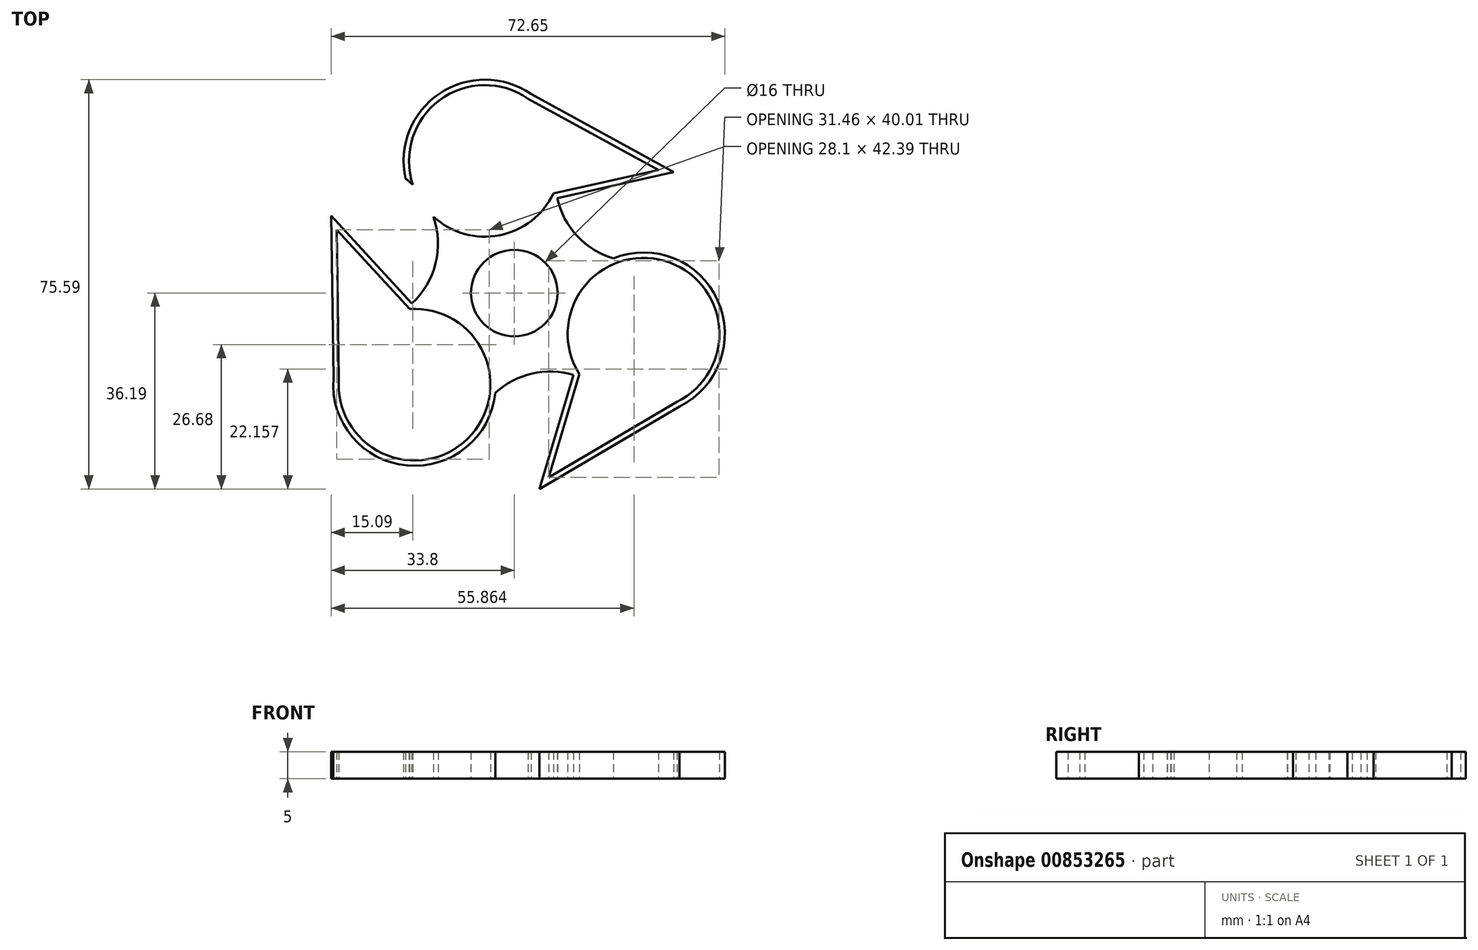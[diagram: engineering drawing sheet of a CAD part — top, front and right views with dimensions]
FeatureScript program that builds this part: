
annotation { "Feature Type Name" : "Feature", "Feature Type Description" : "" }
export const myFeature = defineFeature(function(context is Context, id is Id, definition is map)
    precondition{}
    {
        {
            var Q0;
            Q0=qCreatedBy(makeId("Top.planeOp"),FACE);
            var sketch = newSketch(context, id + "F0", { "sketchPlane" : qUnion([Q0])});
            skCircle(sketch, "E0", {"center": v(0, 0) * mm, "radius": 8 * mm});
            skCircle(sketch, "E1.cCircle", {"center": v(0, 0) * mm, "radius": 10 * mm, "construction": true});
            skLineSegment(sketch, "E1.0", {"start": v(-4.34, 19.52) * mm, "end": v(19.08, -6) * mm, "construction": true});
            skLineSegment(sketch, "E1.1", {"start": v(19.08, -6) * mm, "end": v(-14.73, -13.52) * mm, "construction": true});
            skLineSegment(sketch, "E1.2", {"start": v(-14.73, -13.52) * mm, "end": v(-4.34, 19.52) * mm, "construction": true});
            skPoint(sketch, "E1.0.midPoint", {"position": v(7.37, 6.76) * mm});
            skLineSegment(sketch, "E2", {"start": v(0, 0) * mm, "end": v(-9.6, 43.12) * mm, "construction": true});
            skLineSegment(sketch, "E3", {"start": v(0, 0) * mm, "end": v(53.7, -16.88) * mm, "construction": true});
            skLineSegment(sketch, "E4", {"start": v(0, 0) * mm, "end": v(-29.05, -26.67) * mm, "construction": true});
            skCircle(sketch, "E5", {"center": v(-5.43, 24.4) * mm, "radius": 15 * mm});
            skCircle(sketch, "E6", {"center": v(23.85, -7.5) * mm, "radius": 15 * mm});
            skCircle(sketch, "E7", {"center": v(-18.42, -16.9) * mm, "radius": 15 * mm});
            skLineSegment(sketch, "E8", {"start": v(-5.43, 24.4) * mm, "end": v(14.72, 28.89) * mm, "construction": true});
            skLineSegment(sketch, "E9", {"start": v(14.72, 28.89) * mm, "end": v(-26.3, 19.76) * mm, "construction": true});
            skLineSegment(sketch, "E10", {"start": v(-18.42, -16.9) * mm, "end": v(-38.8, 5.3) * mm, "construction": true});
            skLineSegment(sketch, "E11", {"start": v(-38.8, 5.3) * mm, "end": v(-1.77, -35.05) * mm, "construction": true});
            skLineSegment(sketch, "E12", {"start": v(23.85, -7.5) * mm, "end": v(30.7, 15.55) * mm, "construction": true});
            skLineSegment(sketch, "E13", {"start": v(30.7, 15.55) * mm, "end": v(16.82, -31.15) * mm, "construction": true});
            skArc(sketch, "E14", {"start": v(9.21, 27.66) * mm, "mid": v(11.46, 10.71) * mm, "end": v(28.12, 6.88) * mm});
            skArc(sketch, "E15", {"start": v(-28.56, -5.85) * mm, "mid": v(-14.75, 4.64) * mm, "end": v(-20.07, 21.14) * mm});
            skArc(sketch, "E16", {"start": v(19.58, -21.88) * mm, "mid": v(3.45, -14.83) * mm, "end": v(-8.28, -27.96) * mm});
            skCircle(sketch, "E17", {"center": v(-5.43, 24.4) * mm, "radius": 14 * mm});
            skCircle(sketch, "E18", {"center": v(23.85, -7.5) * mm, "radius": 14 * mm});
            skCircle(sketch, "E19", {"center": v(-18.42, -16.9) * mm, "radius": 14 * mm});
            skLineSegment(sketch, "E20", {"start": v(10.92, -15.1) * mm, "end": v(4.65, -36.2) * mm});
            skLineSegment(sketch, "E21", {"start": v(4.65, -36.2) * mm, "end": v(30.5, -20.95) * mm});
            skLineSegment(sketch, "E22", {"start": v(-18.92, -1.91) * mm, "end": v(-33.8, 14.3) * mm});
            skLineSegment(sketch, "E23", {"start": v(-33.8, 14.3) * mm, "end": v(-33.37, -15.7) * mm});
            skLineSegment(sketch, "E24", {"start": v(7.91, 17.55) * mm, "end": v(29.39, 22.33) * mm});
            skLineSegment(sketch, "E25", {"start": v(29.39, 22.33) * mm, "end": v(3.08, 36.75) * mm});
            skLineSegment(sketch, "E26", {"start": v(2.56, 35.9) * mm, "end": v(26.58, 22.73) * mm});
            skLineSegment(sketch, "E27", {"start": v(26.58, 22.73) * mm, "end": v(7.23, 18.42) * mm});
            skLineSegment(sketch, "E28", {"start": v(-32.37, -15.74) * mm, "end": v(-32.76, 11.69) * mm});
            skLineSegment(sketch, "E29", {"start": v(-32.76, 11.69) * mm, "end": v(-19.34, -2.94) * mm});
            skLineSegment(sketch, "E30", {"start": v(30.02, -20.07) * mm, "end": v(6.34, -34.04) * mm});
            skLineSegment(sketch, "E31", {"start": v(6.34, -34.04) * mm, "end": v(12, -14.96) * mm});
            skSolve(sketch);
        }
        {
            var Q0;
            {var subQ5=sQuery(id+"F0.wireOp",EDGE,"E6");var subQ6=makeQuery(id+"F0.imprint","INTERSECT",VERTEX,{"derivedFrom":[subQ5,sQuery(id+"F0.wireOp",EDGE,"E21")]});Q0=makeQuery(id+"F0.imprint","IMPRINT",FACE,{"disambiguationData":[TD([[makeQuery(id+"F0.imprint","IMPRINT",EDGE,{"disambiguationData":[TD([[subQ6,1.0]])],"derivedFrom":subQ5}),1.0]])]});}
            var Q1;
            {var subQ0=sQuery(id+"F0.wireOp",EDGE,"E20");Q1=makeQuery(id+"F0.imprint","IMPRINT",FACE,{"disambiguationData":[TD([[makeQuery(id+"F0.imprint","IMPRINT",EDGE,{"derivedFrom":subQ0}),1.0]])]});}
            var Q2;
            {var subQ0=sQuery(id+"F0.wireOp",EDGE,"E14");var subQ1=sQuery(id+"F0.wireOp",EDGE,"E6");var subQ2=makeQuery(id+"F0.imprint","INTERSECT",VERTEX,{"disambiguationData":[OD(0.0)],"derivedFrom":[subQ1,subQ0]});Q2=makeQuery(id+"F0.imprint","IMPRINT",FACE,{"disambiguationData":[TD([[makeQuery(id+"F0.imprint","IMPRINT",EDGE,{"disambiguationData":[TD([[subQ2,-1.0]])],"derivedFrom":subQ1}),1.0]])]});}
            var Q3;
            {var subQ1=sQuery(id+"F0.wireOp",EDGE,"E6");var subQ3=sQuery(id+"F0.wireOp",EDGE,"E31");var subQ4=makeQuery(id+"F0.imprint","INTERSECT",VERTEX,{"derivedFrom":[subQ1,subQ3]});Q3=makeQuery(id+"F0.imprint","IMPRINT",FACE,{"disambiguationData":[TD([[makeQuery(id+"F0.imprint","IMPRINT",EDGE,{"disambiguationData":[TD([[subQ4,-1.0]])],"derivedFrom":subQ3}),1.0]])]});}
            var Q4;
            {var subQ3=sQuery(id+"F0.wireOp",EDGE,"E14");var subQ6=sQuery(id+"F0.wireOp",EDGE,"E6");var subQ8=makeQuery(id+"F0.imprint","INTERSECT",VERTEX,{"disambiguationData":[OD(1.0)],"derivedFrom":[subQ6,subQ3]});Q4=makeQuery(id+"F0.imprint","IMPRINT",FACE,{"disambiguationData":[TD([[makeQuery(id+"F0.imprint","IMPRINT",EDGE,{"disambiguationData":[TD([[subQ8,-1.0]])],"derivedFrom":subQ3}),-1.0]])]});}
            var Q5;
            {var subQ1=sQuery(id+"F0.wireOp",EDGE,"E24");Q5=makeQuery(id+"F0.imprint","IMPRINT",FACE,{"disambiguationData":[TD([[makeQuery(id+"F0.imprint","IMPRINT",EDGE,{"derivedFrom":subQ1}),1.0]])]});}
            var Q6;
            {var subQ1=sQuery(id+"F0.wireOp",EDGE,"E5");var subQ3=sQuery(id+"F0.wireOp",EDGE,"E27");var subQ4=makeQuery(id+"F0.imprint","INTERSECT",VERTEX,{"derivedFrom":[subQ1,subQ3]});Q6=makeQuery(id+"F0.imprint","IMPRINT",FACE,{"disambiguationData":[TD([[makeQuery(id+"F0.imprint","IMPRINT",EDGE,{"disambiguationData":[TD([[subQ4,-1.0]])],"derivedFrom":subQ3}),1.0]])]});}
            var Q7;
            {var subQ3=sQuery(id+"F0.wireOp",EDGE,"E15");var subQ6=sQuery(id+"F0.wireOp",EDGE,"E5");var subQ8=makeQuery(id+"F0.imprint","INTERSECT",VERTEX,{"disambiguationData":[OD(1.0)],"derivedFrom":[subQ6,subQ3]});Q7=makeQuery(id+"F0.imprint","IMPRINT",FACE,{"disambiguationData":[TD([[makeQuery(id+"F0.imprint","IMPRINT",EDGE,{"disambiguationData":[TD([[subQ8,-1.0]])],"derivedFrom":subQ3}),-1.0]])]});}
            var Q8;
            {var subQ1=sQuery(id+"F0.wireOp",EDGE,"E5");var subQ3=makeQuery(id+"F0.imprint","INTERSECT",VERTEX,{"derivedFrom":[subQ1,sQuery(id+"F0.wireOp",EDGE,"E25")]});Q8=makeQuery(id+"F0.imprint","IMPRINT",FACE,{"disambiguationData":[TD([[makeQuery(id+"F0.imprint","IMPRINT",EDGE,{"disambiguationData":[TD([[subQ3,1.0]])],"derivedFrom":subQ1}),1.0]])]});}
            var Q9;
            {var subQ0=sQuery(id+"F0.wireOp",EDGE,"E15");var subQ1=sQuery(id+"F0.wireOp",EDGE,"E5");var subQ2=makeQuery(id+"F0.imprint","INTERSECT",VERTEX,{"disambiguationData":[OD(0.0)],"derivedFrom":[subQ1,subQ0]});Q9=makeQuery(id+"F0.imprint","IMPRINT",FACE,{"disambiguationData":[TD([[makeQuery(id+"F0.imprint","IMPRINT",EDGE,{"disambiguationData":[TD([[subQ2,-1.0]])],"derivedFrom":subQ1}),1.0]])]});}
            var Q10;
            {var subQ0=sQuery(id+"F0.wireOp",EDGE,"E16");var subQ1=sQuery(id+"F0.wireOp",EDGE,"E7");var subQ2=makeQuery(id+"F0.imprint","INTERSECT",VERTEX,{"disambiguationData":[OD(0.0)],"derivedFrom":[subQ1,subQ0]});Q10=makeQuery(id+"F0.imprint","IMPRINT",FACE,{"disambiguationData":[TD([[makeQuery(id+"F0.imprint","IMPRINT",EDGE,{"disambiguationData":[TD([[subQ2,-1.0]])],"derivedFrom":subQ1}),1.0]])]});}
            var Q11;
            {var subQ5=sQuery(id+"F0.wireOp",EDGE,"E7");var subQ7=makeQuery(id+"F0.imprint","INTERSECT",VERTEX,{"derivedFrom":[subQ5,sQuery(id+"F0.wireOp",EDGE,"E23")]});Q11=makeQuery(id+"F0.imprint","IMPRINT",FACE,{"disambiguationData":[TD([[makeQuery(id+"F0.imprint","IMPRINT",EDGE,{"disambiguationData":[TD([[subQ7,1.0]])],"derivedFrom":subQ5}),1.0]])]});}
            var Q12;
            {var subQ1=sQuery(id+"F0.wireOp",EDGE,"E22");Q12=makeQuery(id+"F0.imprint","IMPRINT",FACE,{"disambiguationData":[TD([[makeQuery(id+"F0.imprint","IMPRINT",EDGE,{"derivedFrom":subQ1}),1.0]])]});}
            var Q13;
            {var subQ1=sQuery(id+"F0.wireOp",EDGE,"E7");var subQ3=sQuery(id+"F0.wireOp",EDGE,"E29");var subQ4=makeQuery(id+"F0.imprint","INTERSECT",VERTEX,{"derivedFrom":[subQ1,subQ3]});Q13=makeQuery(id+"F0.imprint","IMPRINT",FACE,{"disambiguationData":[TD([[makeQuery(id+"F0.imprint","IMPRINT",EDGE,{"disambiguationData":[TD([[subQ4,-1.0]])],"derivedFrom":subQ3}),1.0]])]});}
            var Q14;
            {var subQ3=sQuery(id+"F0.wireOp",EDGE,"E16");var subQ5=sQuery(id+"F0.wireOp",EDGE,"E7");var subQ6=makeQuery(id+"F0.imprint","INTERSECT",VERTEX,{"disambiguationData":[OD(1.0)],"derivedFrom":[subQ5,subQ3]});Q14=makeQuery(id+"F0.imprint","IMPRINT",FACE,{"disambiguationData":[TD([[makeQuery(id+"F0.imprint","IMPRINT",EDGE,{"disambiguationData":[TD([[subQ6,-1.0]])],"derivedFrom":subQ3}),-1.0]])]});}
            var Q15;
            Q15=makeQuery(id+"F0.imprint","IMPRINT",FACE,{"disambiguationData":[TD([[makeQuery(id+"F0.imprint","IMPRINT",EDGE,{"derivedFrom":sQuery(id+"F0.wireOp",EDGE,"E0")}),-1.0]])]});
            extrude(context, id + "F1", {"entities" : qUnion([Q0, Q1, Q2, Q3, Q4, Q5, Q6, Q7, Q8, Q9, Q10, Q11, Q12, Q13, Q14, Q15]), "depth" : 5 * mm, "offsetDistance" : 25 * mm});
        }
    });
